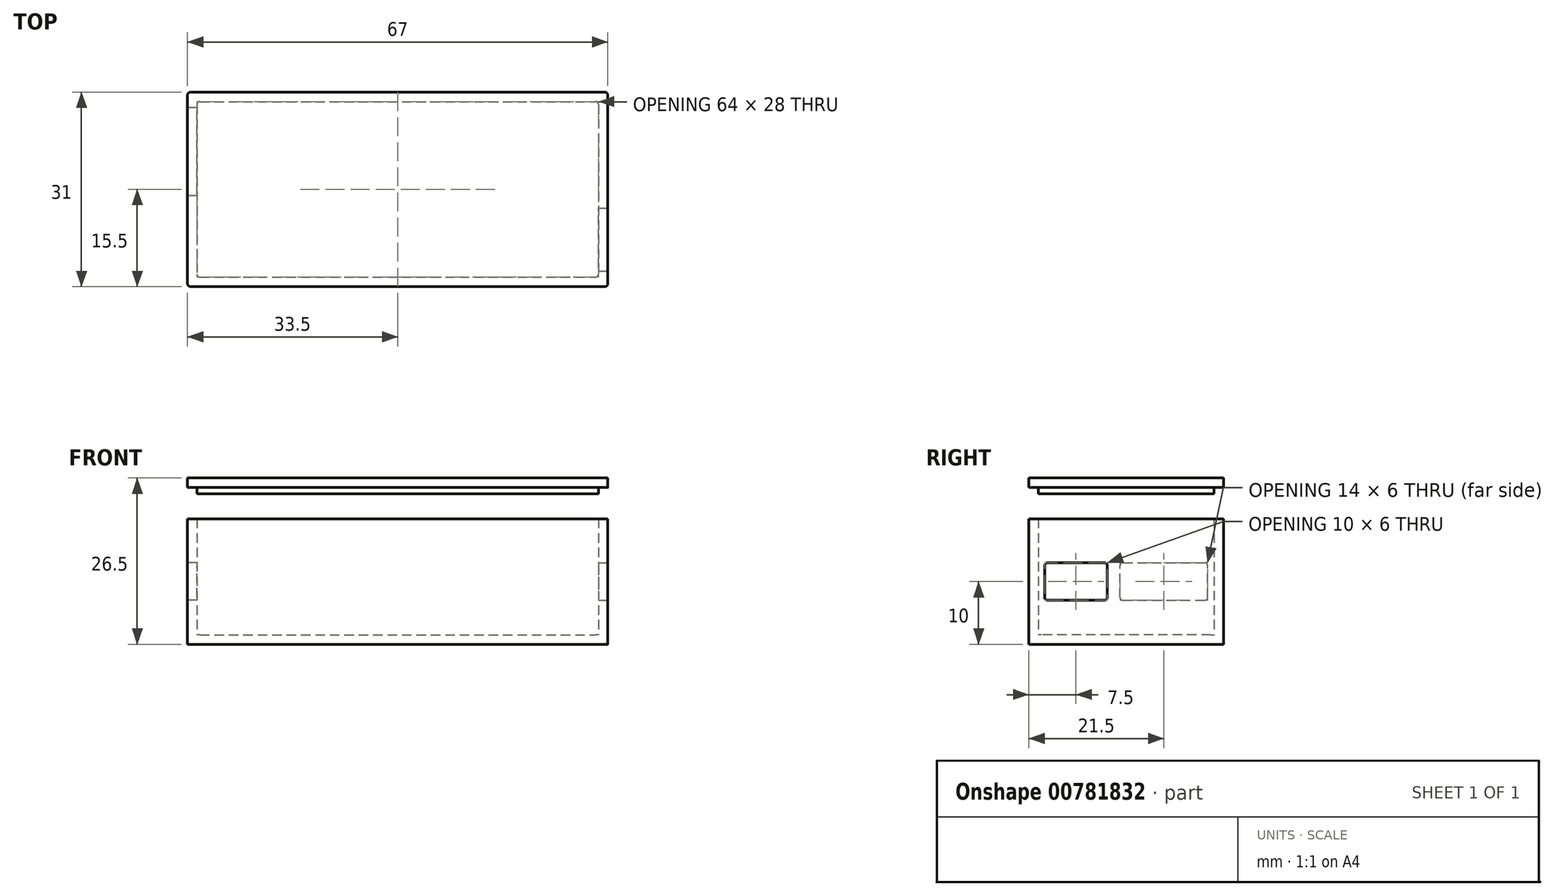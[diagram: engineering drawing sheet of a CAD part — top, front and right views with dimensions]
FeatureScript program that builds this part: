
annotation { "Feature Type Name" : "Feature", "Feature Type Description" : "" }
export const myFeature = defineFeature(function(context is Context, id is Id, definition is map)
    precondition{}
    {
        {
            var Q0;
            Q0=qCreatedBy(makeId("Top.planeOp"),FACE);
            var sketch = newSketch(context, id + "F0", { "sketchPlane" : qUnion([Q0])});
            skLineSegment(sketch, "E0.bottom", {"start": v(-32, 14) * mm, "end": v(32, 14) * mm});
            skLineSegment(sketch, "E0.top", {"start": v(-32, -14) * mm, "end": v(32, -14) * mm});
            skLineSegment(sketch, "E0.left", {"start": v(-32, 14) * mm, "end": v(-32, -14) * mm});
            skLineSegment(sketch, "E0.right", {"start": v(32, 14) * mm, "end": v(32, -14) * mm});
            skLineSegment(sketch, "E1.0", {"start": v(-33.5, 15.5) * mm, "end": v(33.5, 15.5) * mm});
            skLineSegment(sketch, "E1.1", {"start": v(-33.5, 15.5) * mm, "end": v(-33.5, -15.5) * mm});
            skLineSegment(sketch, "E1.2", {"start": v(-33.5, -15.5) * mm, "end": v(33.5, -15.5) * mm});
            skLineSegment(sketch, "E1.3", {"start": v(33.5, 15.5) * mm, "end": v(33.5, -15.5) * mm});
            skSolve(sketch);
        }
        {
            var Q0;
            Q0=makeQuery(id+"F0.imprint","IMPRINT",FACE,{"disambiguationData":[TD([[makeQuery(id+"F0.imprint","IMPRINT",EDGE,{"derivedFrom":sQuery(id+"F0.wireOp",EDGE,"E0.bottom")}),-1.0]])]});
            extrude(context, id + "F1", {"entities" : qUnion([Q0]), "depth" : 1.5 * mm, "offsetDistance" : 25 * mm});
        }
        {
            var Q0;
            Q0=makeQuery(id+"F0.imprint","IMPRINT",FACE,{"disambiguationData":[TD([[makeQuery(id+"F0.imprint","IMPRINT",EDGE,{"derivedFrom":sQuery(id+"F0.wireOp",EDGE,"E0.bottom")}),1.0]])]});
            extrude(context, id + "F2", {"entities" : qUnion([Q0]), "operationType" : NewBodyOperationType.ADD, "depth" : 20 * mm, "offsetDistance" : 25 * mm});
        }
        {
            var Q0;
            Q0=makeQuery(id+"F2.opExtrude","SWEPT_FACE",FACE,{"disambiguationData":[OSD([sQuery(id+"F0.wireOp",EDGE,"E1.3")])]});
            var sketch = newSketch(context, id + "F3", { "sketchPlane" : qUnion([Q0])});
            skLineSegment(sketch, "E2.bottom", {"start": v(-13, 13) * mm, "end": v(-3, 13) * mm});
            skLineSegment(sketch, "E2.top", {"start": v(-13, 7) * mm, "end": v(-3, 7) * mm});
            skLineSegment(sketch, "E2.left", {"start": v(-13, 13) * mm, "end": v(-13, 7) * mm});
            skLineSegment(sketch, "E2.right", {"start": v(-3, 13) * mm, "end": v(-3, 7) * mm});
            skSolve(sketch);
        }
        {
            var Q0;
            Q0=makeQuery(id+"F3.imprint","IMPRINT",FACE,{"disambiguationData":[TD([[makeQuery(id+"F3.imprint","IMPRINT",EDGE,{"derivedFrom":sQuery(id+"F3.wireOp",EDGE,"0jKeejQD-wYWq-uJB9-aREA-mnuBLysYweoR")}),1.0]])]});
            var Q1;
            Q1=makeQuery(id+"F3.imprint","IMPRINT",FACE,{"disambiguationData":[TD([[makeQuery(id+"F3.imprint","IMPRINT",EDGE,{"derivedFrom":sQuery(id+"F3.wireOp",EDGE,"YXOnBARd-7jkv-5pix-mfMH-BnCf1fA0ZYbE")}),1.0]])]});
            var Q2;
            Q2=makeQuery(id+"F3.imprint","IMPRINT",FACE,{"disambiguationData":[TD([[makeQuery(id+"F3.imprint","IMPRINT",EDGE,{"derivedFrom":sQuery(id+"F3.wireOp",EDGE,"E2.bottom")}),-1.0]])]});
            extrude(context, id + "F4", {"entities" : qUnion([Q0, Q1, Q2]), "operationType" : NewBodyOperationType.REMOVE, "oppositeDirection" : true, "depth" : 25 * mm, "offsetDistance" : 25 * mm});
        }
        {
            var Q0;
            Q0=makeQuery(id+"F2.opExtrude","SWEPT_FACE",FACE,{"disambiguationData":[OSD([sQuery(id+"F0.wireOp",EDGE,"E1.1")])]});
            var sketch = newSketch(context, id + "F5", { "sketchPlane" : qUnion([Q0])});
            skLineSegment(sketch, "E3.bottom", {"start": v(-13, 13) * mm, "end": v(1, 13) * mm});
            skLineSegment(sketch, "E3.top", {"start": v(-13, 7) * mm, "end": v(1, 7) * mm});
            skLineSegment(sketch, "E3.left", {"start": v(-13, 13) * mm, "end": v(-13, 7) * mm});
            skLineSegment(sketch, "E3.right", {"start": v(1, 13) * mm, "end": v(1, 7) * mm});
            skSolve(sketch);
        }
        {
            var Q0;
            Q0=makeQuery(id+"F5.imprint","IMPRINT",FACE,{"disambiguationData":[TD([[makeQuery(id+"F5.imprint","IMPRINT",EDGE,{"derivedFrom":sQuery(id+"F5.wireOp",EDGE,"E3.bottom")}),-1.0]])]});
            extrude(context, id + "F6", {"entities" : qUnion([Q0]), "operationType" : NewBodyOperationType.REMOVE, "oppositeDirection" : true, "depth" : 25 * mm, "offsetDistance" : 25 * mm});
        }
        {
            var Q0;
            Q0=makeQuery(id+"F6.boolean.opBoolean","COPY",EDGE,{"derivedFrom":makeQuery(id+"F6.opExtrude","SWEPT_EDGE",EDGE,{"disambiguationData":[OSD([sQuery(id+"F5.wireOp",EDGE,"E3.bottom"),sQuery(id+"F5.wireOp",EDGE,"E3.left")])]})});
            var Q1;
            Q1=makeQuery(id+"F6.boolean.opBoolean","COPY",EDGE,{"derivedFrom":makeQuery(id+"F6.opExtrude","SWEPT_EDGE",EDGE,{"disambiguationData":[OSD([sQuery(id+"F5.wireOp",EDGE,"E3.top"),sQuery(id+"F5.wireOp",EDGE,"E3.left")])]})});
            var Q2;
            Q2=makeQuery(id+"F6.boolean.opBoolean","COPY",EDGE,{"derivedFrom":makeQuery(id+"F6.opExtrude","SWEPT_EDGE",EDGE,{"disambiguationData":[OSD([sQuery(id+"F5.wireOp",EDGE,"E3.bottom"),sQuery(id+"F5.wireOp",EDGE,"E3.right")])]})});
            var Q3;
            Q3=makeQuery(id+"F6.boolean.opBoolean","COPY",EDGE,{"derivedFrom":makeQuery(id+"F6.opExtrude","SWEPT_EDGE",EDGE,{"disambiguationData":[OSD([sQuery(id+"F5.wireOp",EDGE,"E3.top"),sQuery(id+"F5.wireOp",EDGE,"E3.right")])]})});
            var Q4;
            Q4=makeQuery(id+"F4.boolean.opBoolean","COPY",EDGE,{"derivedFrom":makeQuery(id+"F4.opExtrude","SWEPT_EDGE",EDGE,{"disambiguationData":[OSD([sQuery(id+"F3.wireOp",EDGE,"E2.bottom"),sQuery(id+"F3.wireOp",EDGE,"E2.left")])]})});
            var Q5;
            Q5=makeQuery(id+"F4.boolean.opBoolean","COPY",EDGE,{"derivedFrom":makeQuery(id+"F4.opExtrude","SWEPT_EDGE",EDGE,{"disambiguationData":[OSD([sQuery(id+"F3.wireOp",EDGE,"E2.bottom"),sQuery(id+"F3.wireOp",EDGE,"E2.right")])]})});
            var Q6;
            Q6=makeQuery(id+"F4.boolean.opBoolean","COPY",EDGE,{"derivedFrom":makeQuery(id+"F4.opExtrude","SWEPT_EDGE",EDGE,{"disambiguationData":[OSD([sQuery(id+"F3.wireOp",EDGE,"E2.top"),sQuery(id+"F3.wireOp",EDGE,"E2.left")])]})});
            var Q7;
            Q7=makeQuery(id+"F4.boolean.opBoolean","COPY",EDGE,{"derivedFrom":makeQuery(id+"F4.opExtrude","SWEPT_EDGE",EDGE,{"disambiguationData":[OSD([sQuery(id+"F3.wireOp",EDGE,"E2.top"),sQuery(id+"F3.wireOp",EDGE,"E2.right")])]})});
            fillet(context, id + "F7", {"entities" : qUnion([Q0, Q1, Q2, Q3, Q4, Q5, Q6, Q7]), "radius" : .5 * mm, "tangentPropagation" : true, "allowEdgeOverflow" : false});
        }
        {
            var Q0;
            Q0=makeQuery(id+"F4.boolean.opBoolean","COPY",EDGE,{"derivedFrom":makeQuery(id+"F4.opExtrude","CAP_EDGE",EDGE,{"disambiguationData":[OSD([sQuery(id+"F3.wireOp",EDGE,"YXOnBARd-7jkv-5pix-mfMH-BnCf1fA0ZYbE")])],"isStart":true})});
            var Q1;
            Q1=makeQuery(id+"F4.boolean.opBoolean","COPY",EDGE,{"derivedFrom":makeQuery(id+"F4.opExtrude","CAP_EDGE",EDGE,{"disambiguationData":[OSD([sQuery(id+"F3.wireOp",EDGE,"0jKeejQD-wYWq-uJB9-aREA-mnuBLysYweoR")])],"isStart":true})});
            var Q2;
            Q2=makeQuery(id+"F2.opExtrude","SWEPT_EDGE",EDGE,{"disambiguationData":[OSD([sQuery(id+"F0.wireOp",EDGE,"E1.1"),sQuery(id+"F0.wireOp",EDGE,"E1.2")])]});
            var Q3;
            Q3=makeQuery(id+"F2.opExtrude","SWEPT_EDGE",EDGE,{"disambiguationData":[OSD([sQuery(id+"F0.wireOp",EDGE,"E1.0"),sQuery(id+"F0.wireOp",EDGE,"E1.1")])]});
            var Q4;
            Q4=makeQuery(id+"F2.opExtrude","SWEPT_EDGE",EDGE,{"disambiguationData":[OSD([sQuery(id+"F0.wireOp",EDGE,"E1.2"),sQuery(id+"F0.wireOp",EDGE,"E1.3")])]});
            var Q5;
            Q5=makeQuery(id+"F2.opExtrude","SWEPT_EDGE",EDGE,{"disambiguationData":[OSD([sQuery(id+"F0.wireOp",EDGE,"E1.0"),sQuery(id+"F0.wireOp",EDGE,"E1.3")])]});
            var Q6;
            Q6=makeQuery(id+"F2.opExtrude","SWEPT_EDGE",EDGE,{"disambiguationData":[OSD([sQuery(id+"F0.wireOp",EDGE,"E0.top"),sQuery(id+"F0.wireOp",EDGE,"E0.right")])]});
            var Q7;
            Q7=makeQuery(id+"F2.opExtrude","SWEPT_EDGE",EDGE,{"disambiguationData":[OSD([sQuery(id+"F0.wireOp",EDGE,"E0.top"),sQuery(id+"F0.wireOp",EDGE,"E0.left")])]});
            var Q8;
            Q8=makeQuery(id+"F2.opExtrude","SWEPT_EDGE",EDGE,{"disambiguationData":[OSD([sQuery(id+"F0.wireOp",EDGE,"E0.bottom"),sQuery(id+"F0.wireOp",EDGE,"E0.left")])]});
            var Q9;
            Q9=makeQuery(id+"F2.opExtrude","SWEPT_EDGE",EDGE,{"disambiguationData":[OSD([sQuery(id+"F0.wireOp",EDGE,"E0.bottom"),sQuery(id+"F0.wireOp",EDGE,"E0.right")])]});
            fillet(context, id + "F8", {"entities" : qUnion([Q0, Q1, Q2, Q3, Q4, Q5, Q6, Q7, Q8, Q9]), "radius" : .5 * mm, "tangentPropagation" : true, "allowEdgeOverflow" : false});
        }
        {
            var Q0;
            Q0=qCreatedBy(makeId("Top.planeOp"),FACE);
            cPlane(context, id + "F9", {"entities" : qUnion([Q0]), "cplaneType" : CPlaneType.OFFSET, "offset" : 25 * mm, "width" : 150 * mm, "height" : 150 * mm});
        }
        {
            var Q0;
            Q0=qCreatedBy(id+"F9.planeOp",FACE);
            var sketch = newSketch(context, id + "F10", { "sketchPlane" : qUnion([Q0])});
            skLineSegment(sketch, "E4.bottom", {"start": v(-33.5, 15.5) * mm, "end": v(33.5, 15.5) * mm});
            skLineSegment(sketch, "E4.top", {"start": v(-33.5, -15.5) * mm, "end": v(33.5, -15.5) * mm});
            skLineSegment(sketch, "E4.left", {"start": v(-33.5, 15.5) * mm, "end": v(-33.5, -15.5) * mm});
            skLineSegment(sketch, "E4.right", {"start": v(33.5, 15.5) * mm, "end": v(33.5, -15.5) * mm});
            skLineSegment(sketch, "E5.0", {"start": v(-32, 14) * mm, "end": v(32, 14) * mm});
            skLineSegment(sketch, "E5.1", {"start": v(-32, 14) * mm, "end": v(-32, -14) * mm});
            skLineSegment(sketch, "E5.2", {"start": v(-32, -14) * mm, "end": v(32, -14) * mm});
            skLineSegment(sketch, "E5.3", {"start": v(32, 14) * mm, "end": v(32, -14) * mm});
            skSolve(sketch);
        }
        {
            var Q0;
            Q0=makeQuery(id+"F10.imprint","IMPRINT",FACE,{"disambiguationData":[TD([[makeQuery(id+"F10.imprint","IMPRINT",EDGE,{"derivedFrom":sQuery(id+"F10.wireOp",EDGE,"E5.0")}),-1.0]])]});
            var Q1;
            Q1=makeQuery(id+"F10.imprint","IMPRINT",FACE,{"disambiguationData":[TD([[makeQuery(id+"F10.imprint","IMPRINT",EDGE,{"derivedFrom":sQuery(id+"F10.wireOp",EDGE,"E4.bottom")}),-1.0]])]});
            extrude(context, id + "F11", {"entities" : qUnion([Q0, Q1]), "depth" : 1.5 * mm, "offsetDistance" : 25 * mm});
        }
        {
            var Q0;
            Q0=makeQuery(id+"F10.imprint","IMPRINT",FACE,{"disambiguationData":[TD([[makeQuery(id+"F10.imprint","IMPRINT",EDGE,{"derivedFrom":sQuery(id+"F10.wireOp",EDGE,"E5.0")}),-1.0]])]});
            extrude(context, id + "F12", {"entities" : qUnion([Q0]), "operationType" : NewBodyOperationType.ADD, "oppositeDirection" : true, "depth" : 1 * mm, "offsetDistance" : 25 * mm});
        }
        {
            var Q0;
            Q0=makeQuery(id+"F12.opExtrude","SWEPT_EDGE",EDGE,{"disambiguationData":[OSD([sQuery(id+"F10.wireOp",EDGE,"E5.1"),sQuery(id+"F10.wireOp",EDGE,"E5.2")])]});
            var Q1;
            Q1=makeQuery(id+"F11.opExtrude","SWEPT_EDGE",EDGE,{"disambiguationData":[OSD([sQuery(id+"F10.wireOp",EDGE,"E4.top"),sQuery(id+"F10.wireOp",EDGE,"E4.left")])]});
            var Q2;
            Q2=makeQuery(id+"F12.opExtrude","SWEPT_EDGE",EDGE,{"disambiguationData":[OSD([sQuery(id+"F10.wireOp",EDGE,"E5.0"),sQuery(id+"F10.wireOp",EDGE,"E5.1")])]});
            var Q3;
            Q3=makeQuery(id+"F11.opExtrude","SWEPT_EDGE",EDGE,{"disambiguationData":[OSD([sQuery(id+"F10.wireOp",EDGE,"E4.bottom"),sQuery(id+"F10.wireOp",EDGE,"E4.left")])]});
            var Q4;
            Q4=makeQuery(id+"F12.opExtrude","SWEPT_EDGE",EDGE,{"disambiguationData":[OSD([sQuery(id+"F10.wireOp",EDGE,"E5.0"),sQuery(id+"F10.wireOp",EDGE,"E5.3")])]});
            var Q5;
            Q5=makeQuery(id+"F11.opExtrude","SWEPT_EDGE",EDGE,{"disambiguationData":[OSD([sQuery(id+"F10.wireOp",EDGE,"E4.bottom"),sQuery(id+"F10.wireOp",EDGE,"E4.right")])]});
            var Q6;
            Q6=makeQuery(id+"F12.opExtrude","SWEPT_EDGE",EDGE,{"disambiguationData":[OSD([sQuery(id+"F10.wireOp",EDGE,"E5.2"),sQuery(id+"F10.wireOp",EDGE,"E5.3")])]});
            var Q7;
            Q7=makeQuery(id+"F11.opExtrude","SWEPT_EDGE",EDGE,{"disambiguationData":[OSD([sQuery(id+"F10.wireOp",EDGE,"E4.top"),sQuery(id+"F10.wireOp",EDGE,"E4.right")])]});
            fillet(context, id + "F13", {"entities" : qUnion([Q0, Q1, Q2, Q3, Q4, Q5, Q6, Q7]), "radius" : .5 * mm, "tangentPropagation" : true, "allowEdgeOverflow" : false});
        }
    });
